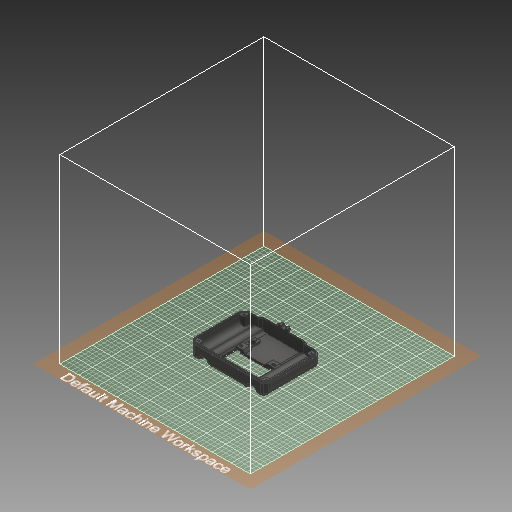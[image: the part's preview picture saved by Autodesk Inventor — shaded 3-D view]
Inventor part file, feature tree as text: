
AUTODESK INVENTOR PART (.ipt)
format: ipt  version: 2019.4 (Build 234330000, 330)  size: 1,575,424 bytes
history: native  units: in
note: dims shown in document units (in); Inventor stores cm internally (conversion verified against a paired STEP export)
features: sketch x17, extrude x13, fillet x8, chamfer x3, move_body x3, direct_edit x2, imported_body x1
ambient origin geometry x8: Origin, YZ Plane, XZ Plane, XY Plane, X Axis, Y Axis, Z Axis, Center Point
bodies: Solid1 (feature_tree)
feature tree (47):
  imported_body  "Base1"
  fillet  "Fillet1"  Radius=0.3937in
  fillet  "Fillet2"  Radius=0.5512in
  fillet  "Fillet3"  Radius=0.1969in
  fillet  "Fillet4"  Radius=0.1969in
  fillet  "Fillet5"  Radius=0.1969in
  sketch  "Sketch1"  dims[d5=0.5906in d6=1.6142in]
  extrude  "Extrusion1"  Depth=1.6142in
  extrude  "Extrusion2"  Depth=1.7717in
  extrude  "Extrusion3"  Depth=0.2362in
  chamfer  "Chamfer1"  Distance=1.6437in
  extrude  "Extrusion4"  Depth=0.5906in
  extrude  "Extrusion5"  Depth=0.5906in
  sketch  "Sketch7"  dims[d16=0.126in d17=1.6437in d18=0.0in]
  chamfer  "Chamfer2"  Distance=0.1969in
  extrude  "Extrusion8"  Depth=0.1969in
  fillet  "Fillet7"  Radius=0.122in
  extrude  "Extrusion9"  Depth=0.0945in TaperAngle=0.0deg
  extrude  "Extrusion10"  Depth=0.3937in
  fillet  "Fillet8"  Radius=0.3937in
  extrude  "Extrusion11"  Depth=0.1969in
  sketch  "Sketch14"  dims[d25=0.5906in]
  extrude  "Extrusion12"  Depth=0.3937in
  extrude  "Extrusion13"  Depth=0.3937in
  extrude  "Extrusion14"  Depth=0.3937in
  direct_edit  "Direct Edit1"
  sketch  "Sketch18"  dims[d37=0.3937in d38=0.3937in d39=0.3937in]
  extrude  "Extrusion15"  Depth=0.1575in TaperAngle=0.0deg
  fillet  "Fillet9"  Radius=0.1378in
  chamfer  "Chamfer3"  Distance=0.1575in
  direct_edit  "Direct Edit2"
  sketch  "Sketch2"  dims[d7=3.2283in d8=1.7717in]
  sketch  "Sketch3"  dims[d9=1.6437in d10=0.0in d12=0.2362in]
  sketch  "Sketch4"  dims[d13=0.2362in]
  sketch  "Sketch5"  dims[d14=0.126in]
  sketch  "Sketch6"  dims[d15=0.126in]
  sketch  "Sketch10"  dims[d19=0.5906in d20=0.5906in]
  sketch  "Sketch11"  dims[d21=0.5906in d22=0.5906in]
  sketch  "Sketch12"  dims[d23=0.2953in]
  sketch  "Sketch13"  dims[d24=0.3937in]
  sketch  "Sketch15"  dims[d26=0.3937in d27=0.1969in d28=0.0in]
  sketch  "Sketch16"  dims[d29=0.1969in d30=0.0787in d31=45.0deg d32=0.122in d33=0.122in]
  sketch  "Sketch17"  dims[d34=0.122in d35=0.0945in d36=0.0in]
  sketch  "Sketch19"  dims[d40=0.3937in d41=0.1969in d42=0.3937in d43=0.3937in d44=0.3937in d45=0.1575in d46=0.0in d47=0.1378in d48=0.0787in d49=45.0deg d61=0.1575in d62=0.0in d63=0.3937in d64=0.3543in d65=0.4528in d68=0.1575in d69=0.0in d70=0.2362in d71=0.2362in d72=0.0787in d73=0.0787in d74=0.1378in d75=0.0in d76=0.1772in d77=0.3051in d78=0.6102in d79=0.0591in d80=0.0591in d81=0.1969in d82=0.0in d83=0.1969in d84=0.1969in d85=0.1969in d86=0.0in d87=0.2362in d88=0.1575in d89=0.1575in d90=0.1575in d91=0.1575in d92=1.4469in d93=0.0in d94=0.315in d95=0.315in d96=0.315in d97=0.315in d98=0.315in d99=0.0in d100=0.7087in d101=0.0in d102=0.0in d103=0.0in d104=0.0394in d105=0.0in d106=0.0in d107=0.0394in d109=0.0039in d110=0.0039in d111=0.3622in d112=0.4606in d113=0.3937in d114=0.0in d115=0.1772in d116=0.1181in d117=0.0787in d118=45.0deg d119=0.0in d120=-0.0079in d121=0.0in]
  move_body  "Move1"
  move_body  "Move2"
  move_body  "Move3"
